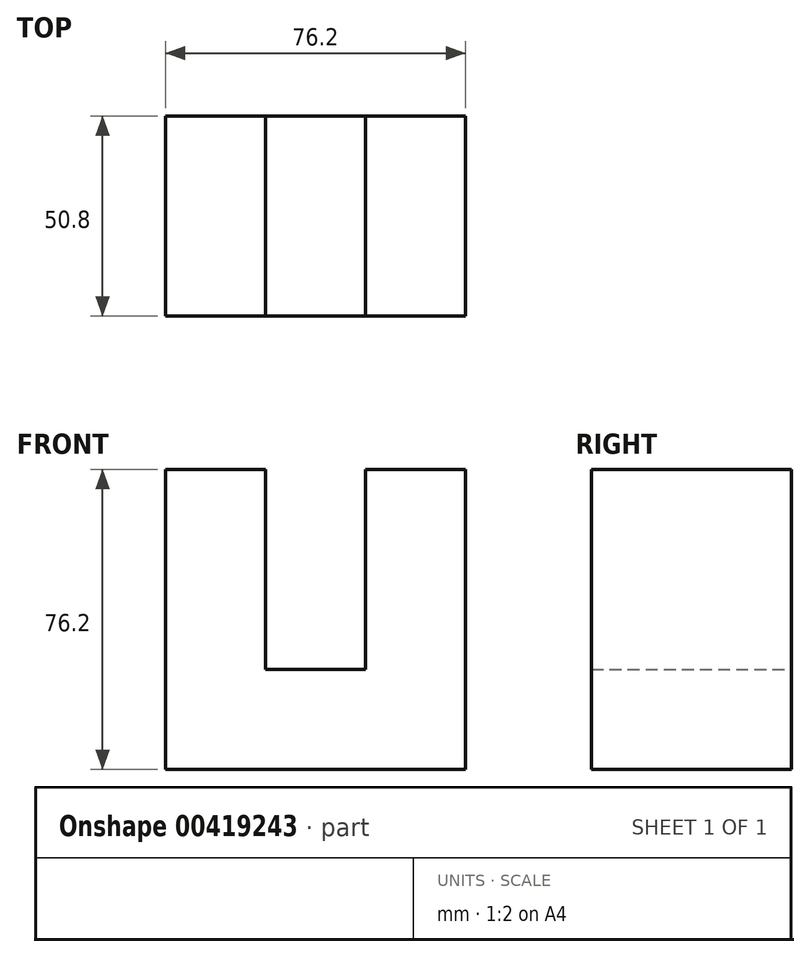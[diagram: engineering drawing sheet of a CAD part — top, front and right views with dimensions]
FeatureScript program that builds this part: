
annotation { "Feature Type Name" : "Feature", "Feature Type Description" : "" }
export const myFeature = defineFeature(function(context is Context, id is Id, definition is map)
    precondition{}
    {
        {
            var Q0;
            Q0=qCreatedBy(makeId("Front.planeOp"),FACE);
            var sketch = newSketch(context, id + "F0", { "sketchPlane" : qUnion([Q0])});
            skLineSegment(sketch, "E0", {"start": v(0, -76.2) * mm, "end": v(-76.2, -76.2) * mm});
            skLineSegment(sketch, "E1", {"start": v(-76.2, -76.2) * mm, "end": v(-76.2, 0) * mm});
            skLineSegment(sketch, "E2", {"start": v(-76.2, 0) * mm, "end": v(-50.8, 0) * mm});
            skLineSegment(sketch, "E3", {"start": v(-50.8, -50.8) * mm, "end": v(-25.4, -50.8) * mm});
            skLineSegment(sketch, "E4", {"start": v(-25.4, -50.8) * mm, "end": v(-25.4, 0) * mm});
            skLineSegment(sketch, "E5", {"start": v(-25.4, 0) * mm, "end": v(0, 0) * mm});
            skLineSegment(sketch, "E6", {"start": v(0, 0) * mm, "end": v(0, -76.2) * mm});
            skLineSegment(sketch, "E7", {"start": v(-50.8, 0) * mm, "end": v(-50.8, -50.8) * mm});
            skSolve(sketch);
        }
        {
            var Q0;
            Q0 = qSketchRegion(id + "F0", true);
            extrude(context, id + "F1", {"entities" : qUnion([Q0]), "depth" : 50.8 * mm});
        }
    });
